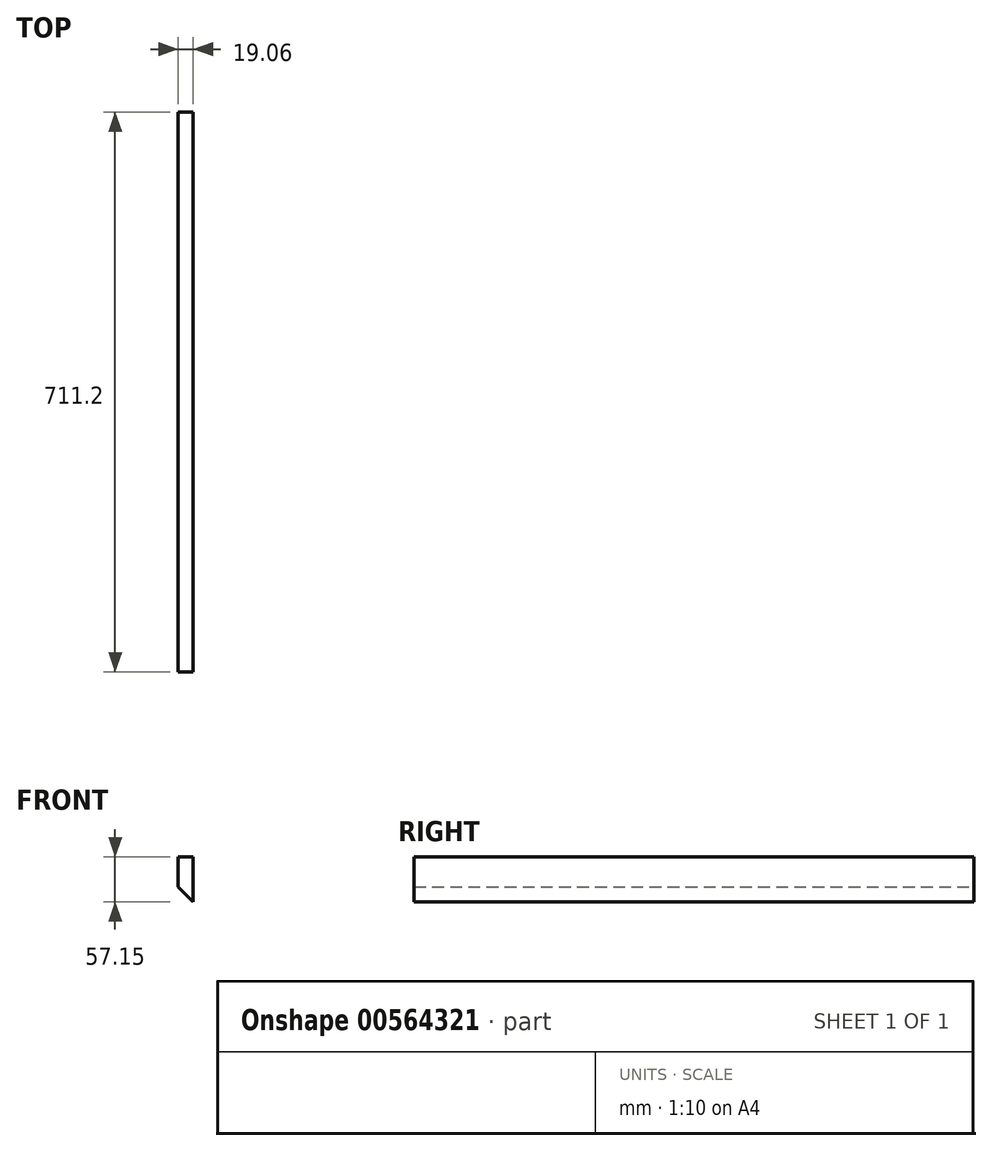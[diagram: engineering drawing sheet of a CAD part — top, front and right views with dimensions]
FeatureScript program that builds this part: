
annotation { "Feature Type Name" : "Feature", "Feature Type Description" : "" }
export const myFeature = defineFeature(function(context is Context, id is Id, definition is map)
    precondition{}
    {
        {
            var Q0;
            Q0=qCreatedBy(makeId("Front.planeOp"),FACE);
            var sketch = newSketch(context, id + "F0", { "sketchPlane" : qUnion([Q0])});
            skLineSegment(sketch, "E0.bottom", {"start": v(-9.53, 23.81) * mm, "end": v(9.53, 23.81) * mm});
            skLineSegment(sketch, "E0.left", {"start": v(-9.53, 23.81) * mm, "end": v(-9.52, -14.29) * mm});
            skLineSegment(sketch, "E0.right", {"start": v(9.52, 23.81) * mm, "end": v(9.53, -33.34) * mm});
            skLineSegment(sketch, "E1", {"start": v(9.52, -33.34) * mm, "end": v(-9.53, -14.29) * mm});
            skSolve(sketch);
        }
        {
            var Q0;
            Q0 = qSketchRegion(id + "F0", true);
            extrude(context, id + "F1", {"entities" : qUnion([Q0]), "depth" : 711.2 * mm, "offsetDistance" : 25.4 * mm});
        }
    });
